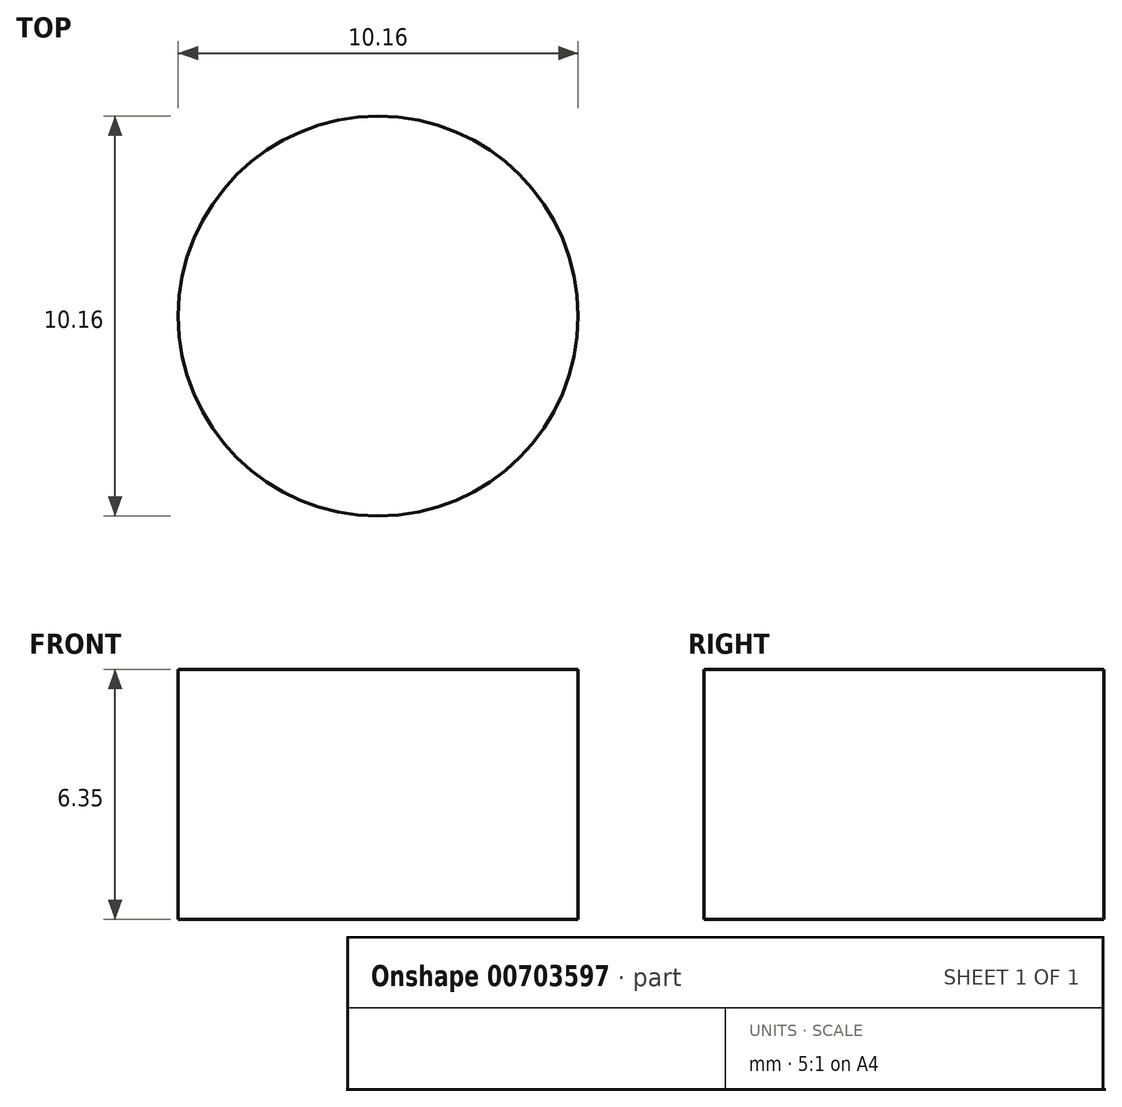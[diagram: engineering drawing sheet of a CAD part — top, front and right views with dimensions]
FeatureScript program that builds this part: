
annotation { "Feature Type Name" : "Feature", "Feature Type Description" : "" }
export const myFeature = defineFeature(function(context is Context, id is Id, definition is map)
    precondition{}
    {
        {
            var Q0;
            Q0=qCreatedBy(makeId("Top.planeOp"),FACE);
            var sketch = newSketch(context, id + "F0", { "sketchPlane" : qUnion([Q0])});
            skCircle(sketch, "E0", {"center": v(0, 0) * mm, "radius": 25.4 * mm});
            skCircle(sketch, "E1", {"center": v(-24.13, 27.94) * mm, "radius": 14.6 * mm});
            skCircle(sketch, "E2.MirrorC", {"center": v(24.13, 27.94) * mm, "radius": 14.6 * mm});
            skSolve(sketch);
        }
        {
            var Q0;
            {var subQ0=sQuery(id+"F0.wireOp",EDGE,"E2.MirrorC");var subQ1=sQuery(id+"F0.wireOp",EDGE,"E0");var subQ2=makeQuery(id+"F0.imprint","INTERSECT",VERTEX,{"disambiguationData":[OD(0.0)],"derivedFrom":[subQ1,subQ0]});Q0=makeQuery(id+"F0.imprint","IMPRINT",FACE,{"disambiguationData":[TD([[makeQuery(id+"F0.imprint","IMPRINT",EDGE,{"disambiguationData":[TD([[subQ2,-1.0]])],"derivedFrom":subQ1}),1.0]])]});}
            var Q1;
            {var subQ0=sQuery(id+"F0.wireOp",EDGE,"E1");var subQ1=sQuery(id+"F0.wireOp",EDGE,"E0");var subQ2=makeQuery(id+"F0.imprint","INTERSECT",VERTEX,{"disambiguationData":[OD(0.0)],"derivedFrom":[subQ1,subQ0]});Q1=makeQuery(id+"F0.imprint","IMPRINT",FACE,{"disambiguationData":[TD([[makeQuery(id+"F0.imprint","IMPRINT",EDGE,{"disambiguationData":[TD([[subQ2,-1.0]])],"derivedFrom":subQ1}),-1.0]])]});}
            var Q2;
            {var subQ0=sQuery(id+"F0.wireOp",EDGE,"E1");var subQ1=sQuery(id+"F0.wireOp",EDGE,"E0");var subQ2=makeQuery(id+"F0.imprint","INTERSECT",VERTEX,{"disambiguationData":[OD(0.0)],"derivedFrom":[subQ1,subQ0]});Q2=makeQuery(id+"F0.imprint","IMPRINT",FACE,{"disambiguationData":[TD([[makeQuery(id+"F0.imprint","IMPRINT",EDGE,{"disambiguationData":[TD([[subQ2,-1.0]])],"derivedFrom":subQ1}),1.0]])]});}
            var Q3;
            {var subQ0=sQuery(id+"F0.wireOp",EDGE,"E2.MirrorC");var subQ1=sQuery(id+"F0.wireOp",EDGE,"E0");var subQ2=makeQuery(id+"F0.imprint","INTERSECT",VERTEX,{"disambiguationData":[OD(0.0)],"derivedFrom":[subQ1,subQ0]});Q3=makeQuery(id+"F0.imprint","IMPRINT",FACE,{"disambiguationData":[TD([[makeQuery(id+"F0.imprint","IMPRINT",EDGE,{"disambiguationData":[TD([[subQ2,1.0]])],"derivedFrom":subQ1}),1.0]])]});}
            var Q4;
            {var subQ0=sQuery(id+"F0.wireOp",EDGE,"E2.MirrorC");var subQ1=sQuery(id+"F0.wireOp",EDGE,"E0");var subQ2=makeQuery(id+"F0.imprint","INTERSECT",VERTEX,{"disambiguationData":[OD(0.0)],"derivedFrom":[subQ1,subQ0]});Q4=makeQuery(id+"F0.imprint","IMPRINT",FACE,{"disambiguationData":[TD([[makeQuery(id+"F0.imprint","IMPRINT",EDGE,{"disambiguationData":[TD([[subQ2,1.0]])],"derivedFrom":subQ1}),-1.0]])]});}
            extrude(context, id + "F1", {"entities" : qUnion([Q0, Q1, Q2, Q3, Q4]), "depth" : 6.35 * mm, "offsetDistance" : 25.4 * mm});
        }
        {
            var Q0;
            Q0=makeQuery(id+"F1.opExtrude","CAP_FACE",FACE,{"disambiguationData":[OSD([sQuery(id+"F0.wireOp",EDGE,"E0"),sQuery(id+"F0.wireOp",EDGE,"E1"),sQuery(id+"F0.wireOp",EDGE,"E2.MirrorC")])],"isStart":false});
            var sketch = newSketch(context, id + "F2", { "sketchPlane" : qUnion([Q0])});
            skSolve(sketch);
        }
        {
            var Q0;
            {var subQ2=sQuery(id+"F0.wireOp",EDGE,"E1");Q0=makeQuery(id+"F2.imprint","IMPRINT",FACE,{"disambiguationData":[TD([[makeQuery(id+"F2.imprint","IMPRINT",EDGE,{"derivedFrom":makeQuery(id+"F1.opExtrude","CAP_EDGE",EDGE,{"disambiguationData":[OSD([subQ2])],"isStart":false})}),1.0]])]});}
            var sketch = newSketch(context, id + "F3", { "sketchPlane" : qUnion([Q0])});
            skCircle(sketch, "E3", {"center": v(0, -5.9) * mm, "radius": 12.25 * mm});
            skLineSegment(sketch, "E4", {"start": v(-12.21, -6.88) * mm, "end": v(12.21, -6.88) * mm});
            skSolve(sketch);
        }
        {
            var Q0;
            {var subQ0=sQuery(id+"F3.wireOp",EDGE,"E4");Q0=makeQuery(id+"F3.imprint","IMPRINT",FACE,{"disambiguationData":[TD([[makeQuery(id+"F3.imprint","IMPRINT",EDGE,{"derivedFrom":subQ0}),-1.0]])]});}
            extrude(context, id + "F4", {"entities" : qUnion([Q0]), "operationType" : NewBodyOperationType.REMOVE, "oppositeDirection" : true, "depth" : 25.4 * mm, "offsetDistance" : 25.4 * mm});
        }
        {
            var Q0;
            {var subQ2=sQuery(id+"F0.wireOp",EDGE,"E1");Q0=makeQuery(id+"F2.imprint","IMPRINT",FACE,{"disambiguationData":[TD([[makeQuery(id+"F2.imprint","IMPRINT",EDGE,{"derivedFrom":makeQuery(id+"F1.opExtrude","CAP_EDGE",EDGE,{"disambiguationData":[OSD([subQ2])],"isStart":false})}),1.0]])]});}
            var sketch = newSketch(context, id + "F5", { "sketchPlane" : qUnion([Q0])});
            skCircle(sketch, "E5", {"center": v(-7.62, 8.36) * mm, "radius": 5.08 * mm});
            skCircle(sketch, "E6.MirrorC", {"center": v(7.62, 8.36) * mm, "radius": 5.08 * mm});
            skSolve(sketch);
        }
        {
            var Q0;
            Q0=makeQuery(id+"F5.imprint","IMPRINT",FACE,{"disambiguationData":[TD([[makeQuery(id+"F5.imprint","IMPRINT",EDGE,{"derivedFrom":sQuery(id+"F5.wireOp",EDGE,"E5")}),1.0]])]});
            var Q1;
            Q1=makeQuery(id+"F5.imprint","IMPRINT",FACE,{"disambiguationData":[TD([[makeQuery(id+"F5.imprint","IMPRINT",EDGE,{"derivedFrom":sQuery(id+"F5.wireOp",EDGE,"E6.MirrorC")}),-1.0]])]});
            extrude(context, id + "F6", {"entities" : qUnion([Q0, Q1]), "operationType" : NewBodyOperationType.REMOVE, "oppositeDirection" : true, "depth" : 25.4 * mm, "offsetDistance" : 25.4 * mm});
        }
    });
